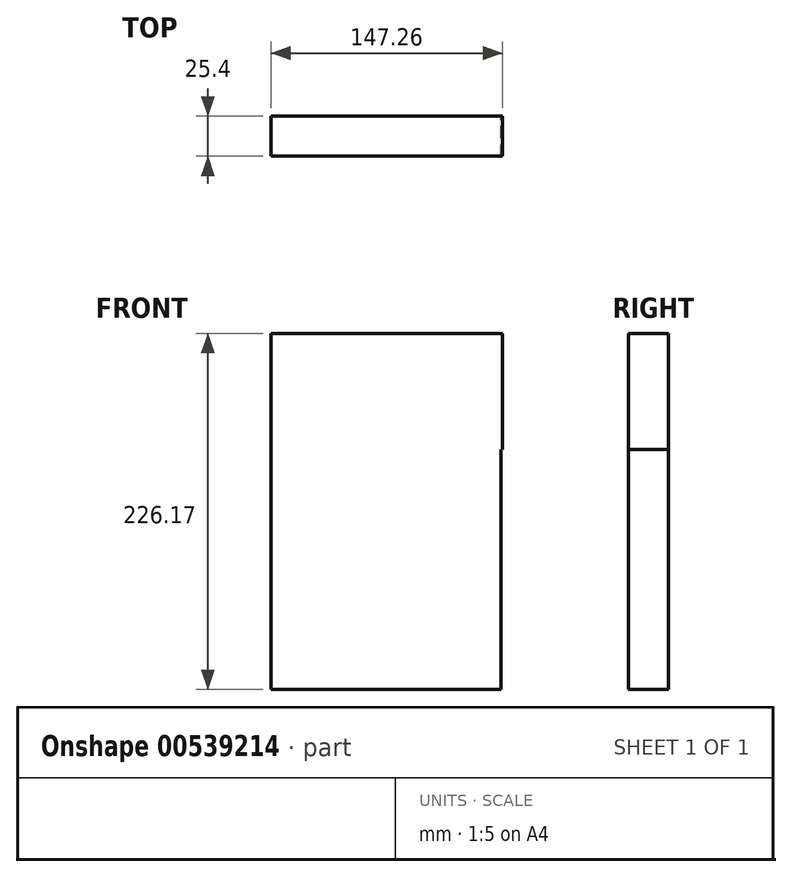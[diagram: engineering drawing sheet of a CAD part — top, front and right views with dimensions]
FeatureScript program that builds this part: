
annotation { "Feature Type Name" : "Feature", "Feature Type Description" : "" }
export const myFeature = defineFeature(function(context is Context, id is Id, definition is map)
    precondition{}
    {
        {
            var Q0;
            Q0=qCreatedBy(makeId("Front.planeOp"),FACE);
            var sketch = newSketch(context, id + "F0", { "sketchPlane" : qUnion([Q0])});
            skLineSegment(sketch, "E0.bottom", {"start": v(0, 0) * mm, "end": v(-73.07, 0) * mm});
            skLineSegment(sketch, "E0.top", {"start": v(0, 73.84) * mm, "end": v(-73.07, 73.84) * mm});
            skLineSegment(sketch, "E0.left", {"start": v(0, 0) * mm, "end": v(0, 73.84) * mm});
            skLineSegment(sketch, "E0.right", {"start": v(-73.07, 0) * mm, "end": v(-73.07, 73.84) * mm});
            skLineSegment(sketch, "E1.bottom", {"start": v(74.2, 73.84) * mm, "end": v(0, 73.84) * mm});
            skLineSegment(sketch, "E1.top", {"start": v(74.2, 0) * mm, "end": v(0, 0) * mm});
            skLineSegment(sketch, "E1.left", {"start": v(74.2, 73.84) * mm, "end": v(74.2, 0) * mm});
            skLineSegment(sketch, "E1.right", {"start": v(0, 73.84) * mm, "end": v(0, 0) * mm});
            skLineSegment(sketch, "E2.bottom", {"start": v(-73.07, 0) * mm, "end": v(73.07, 0) * mm});
            skLineSegment(sketch, "E2.top", {"start": v(-73.07, -152.33) * mm, "end": v(73.07, -152.33) * mm});
            skLineSegment(sketch, "E2.left", {"start": v(-73.07, 0) * mm, "end": v(-73.07, -152.33) * mm});
            skLineSegment(sketch, "E2.right", {"start": v(73.07, 0) * mm, "end": v(73.07, -152.33) * mm});
            skPoint(sketch, "E2.middle", {"position": v(0, -76.16) * mm});
            skSolve(sketch);
        }
        {
            var Q0;
            Q0=makeQuery(id+"F0.imprint","IMPRINT",FACE,{"disambiguationData":[TD([[makeQuery(id+"F0.imprint","IMPRINT",EDGE,{"derivedFrom":sQuery(id+"F0.wireOp",EDGE,"E2.top")}),1.0]])]});
            var Q1;
            Q1=makeQuery(id+"F0.imprint","IMPRINT",FACE,{"disambiguationData":[TD([[makeQuery(id+"F0.imprint","IMPRINT",EDGE,{"derivedFrom":sQuery(id+"F0.wireOp",EDGE,"E1.bottom")}),1.0]])]});
            var Q2;
            Q2=makeQuery(id+"F0.imprint","IMPRINT",FACE,{"disambiguationData":[TD([[makeQuery(id+"F0.imprint","IMPRINT",EDGE,{"derivedFrom":sQuery(id+"F0.wireOp",EDGE,"E0.top")}),1.0]])]});
            extrude(context, id + "F1", {"entities" : qUnion([Q0, Q1, Q2]), "depth" : 25.4 * mm, "offsetDistance" : 25.4 * mm});
        }
    });
